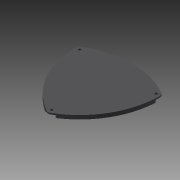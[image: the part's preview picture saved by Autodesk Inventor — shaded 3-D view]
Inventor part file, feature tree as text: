
AUTODESK INVENTOR PART (.ipt)
format: ipt  version: 2013 (Build 170138000, 138)  size: 127,488 bytes
history: native  units: mm
features: extrude x3, sketch x3, fillet x1
ambient origin geometry x8: Origin, YZ Plane, XZ Plane, XY Plane, X Axis, Y Axis, Z Axis, Center Point
bodies: Solid1 (feature_tree)
feature tree (7):
  extrude  "Extrusion1"  Depth=250.0mm
  extrude  "Extrusion2"  Depth=12.5mm TaperAngle=0.0deg
  extrude  "Extrusion8"  Depth=5.0mm TaperAngle=0.0deg
  fillet  "Fillet1"  Radius=8.0mm
  sketch  "Sketch1"  dims[d0=200.0mm d2=250.0mm]
  sketch  "Sketch2"  dims[d3=12.5mm d4=12.5mm d5=0.0mm]
  sketch  "Sketch10"  dims[d6=8.2mm d8=5.0mm d9=0.0mm d44=8.0mm d45=0.0mm d46=5.0mm]
